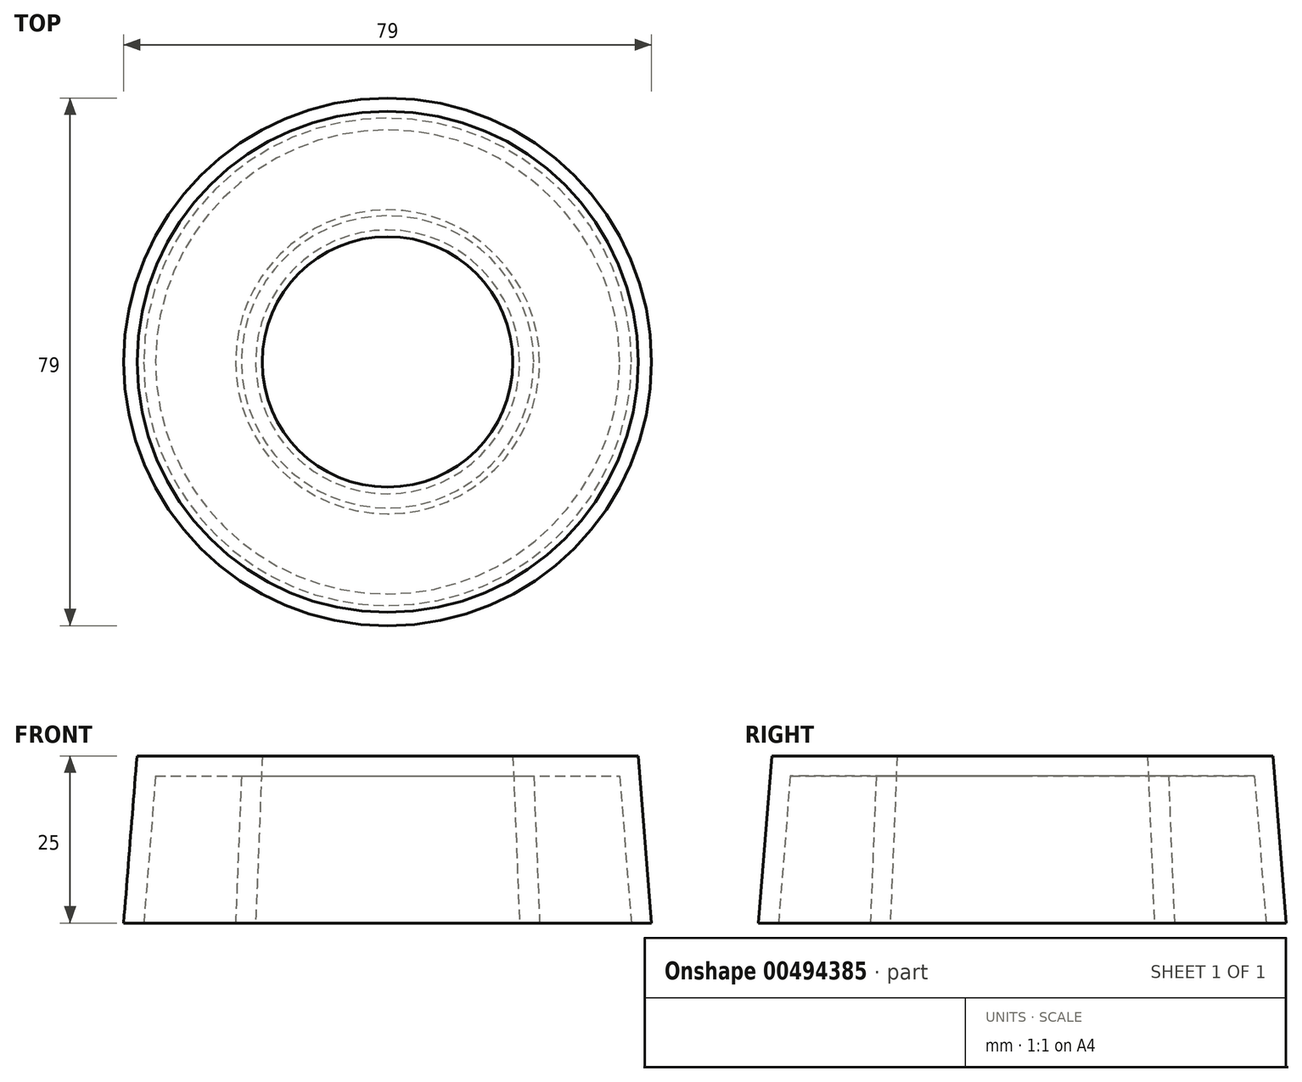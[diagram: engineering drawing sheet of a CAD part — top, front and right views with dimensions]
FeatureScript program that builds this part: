
annotation { "Feature Type Name" : "Feature", "Feature Type Description" : "" }
export const myFeature = defineFeature(function(context is Context, id is Id, definition is map)
    precondition{}
    {
        {
            var Q0;
            Q0=qCreatedBy(makeId("Front.planeOp"),FACE);
            var sketch = newSketch(context, id + "F0", { "sketchPlane" : qUnion([Q0])});
            skLineSegment(sketch, "E0", {"start": v(0, 0) * mm, "end": v(0, 25) * mm});
            skLineSegment(sketch, "E1", {"start": v(0, 25) * mm, "end": v(-37.5, 25) * mm});
            skLineSegment(sketch, "E2", {"start": v(-37.5, 25) * mm, "end": v(-39.5, 0) * mm});
            skLineSegment(sketch, "E3", {"start": v(-39.5, 0) * mm, "end": v(0, 0) * mm});
            skLineSegment(sketch, "E4", {"start": v(-18.75, 25) * mm, "end": v(-19.75, 0) * mm});
            skSolve(sketch);
        }
        {
            var Q0;
            {var subQ0=sQuery(id+"F0.wireOp",EDGE,"E2");Q0=makeQuery(id+"F0.imprint","IMPRINT",FACE,{"disambiguationData":[TD([[makeQuery(id+"F0.imprint","IMPRINT",EDGE,{"derivedFrom":subQ0}),1.0]])]});}
            var Q1;
            Q1=sQuery(id+"F0.wireOp",EDGE,"E0");
            revolve(context, id + "F1", {"entities" : qUnion([Q0]), "axis" : qUnion([Q1]), "revolveType" : RevolveType.FULL});
        }
        {
            var Q0;
            Q0=makeQuery(id+"F1.opRevolve","SWEPT_FACE",FACE,{"disambiguationData":[OSD([sQuery(id+"F0.wireOp",EDGE,"E3")])]});
            shell(context, id + "F2", {"entities" : qUnion([Q0]), "thickness" : 3 * mm});
        }
    });
